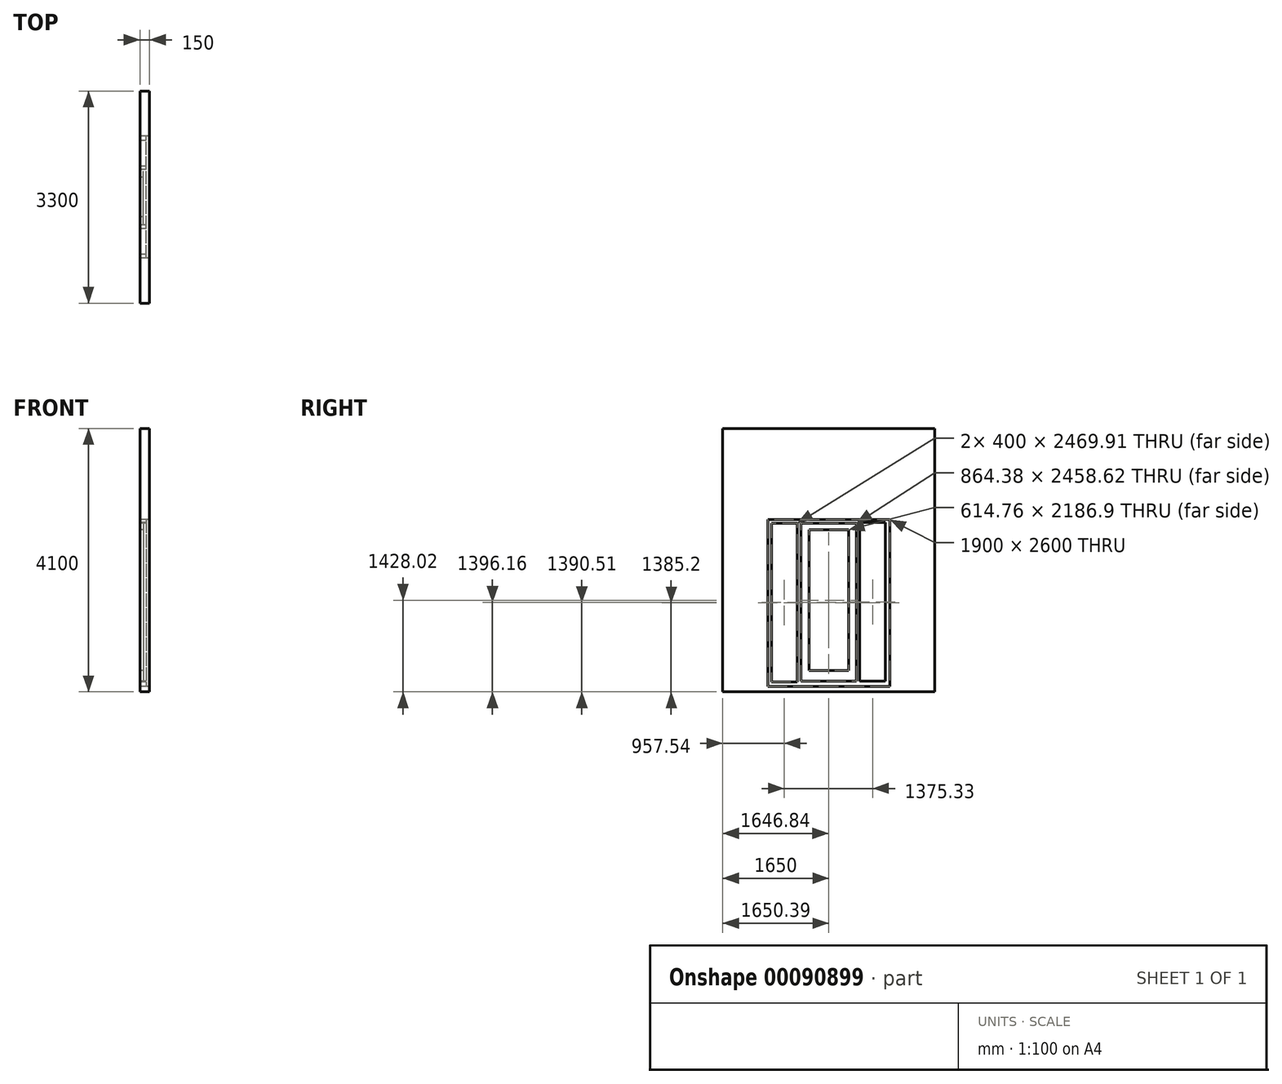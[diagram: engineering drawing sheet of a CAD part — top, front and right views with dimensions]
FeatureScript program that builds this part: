
annotation { "Feature Type Name" : "Feature", "Feature Type Description" : "" }
export const myFeature = defineFeature(function(context is Context, id is Id, definition is map)
    precondition{}
    {
        {
            var Q0;
            Q0=qCreatedBy(makeId("Right.planeOp"),FACE);
            var sketch = newSketch(context, id + "F0", { "sketchPlane" : qUnion([Q0])});
            skLineSegment(sketch, "E0.bottom", {"start": v(-1647.84, 2122.17) * mm, "end": v(1652.16, 2122.17) * mm});
            skLineSegment(sketch, "E0.top", {"start": v(-1647.84, -1977.83) * mm, "end": v(1652.16, -1977.83) * mm});
            skLineSegment(sketch, "E0.left", {"start": v(-1647.84, 2122.17) * mm, "end": v(-1647.84, -1977.83) * mm});
            skLineSegment(sketch, "E0.right", {"start": v(1652.16, 2122.17) * mm, "end": v(1652.16, -1977.83) * mm});
            skLineSegment(sketch, "E1.bottom", {"start": v(-947.84, 707.37) * mm, "end": v(952.16, 707.37) * mm});
            skLineSegment(sketch, "E1.top", {"start": v(-947.84, -1892.63) * mm, "end": v(952.16, -1892.63) * mm});
            skLineSegment(sketch, "E1.left", {"start": v(-947.84, 707.37) * mm, "end": v(-947.84, -1892.63) * mm});
            skLineSegment(sketch, "E1.right", {"start": v(952.16, 707.37) * mm, "end": v(952.16, -1892.63) * mm});
            skLineSegment(sketch, "E2.bottom", {"start": v(-890.3, 647.64) * mm, "end": v(-490.3, 647.64) * mm});
            skLineSegment(sketch, "E2.top", {"start": v(-890.3, -1822.27) * mm, "end": v(-490.3, -1822.27) * mm});
            skLineSegment(sketch, "E2.left", {"start": v(-890.3, 647.64) * mm, "end": v(-890.3, -1822.27) * mm});
            skLineSegment(sketch, "E2.right", {"start": v(-490.3, 647.64) * mm, "end": v(-490.3, -1822.27) * mm});
            skLineSegment(sketch, "E3.bottom", {"start": v(485.03, 658.92) * mm, "end": v(885.03, 658.92) * mm});
            skLineSegment(sketch, "E3.top", {"start": v(485.03, -1810.99) * mm, "end": v(885.03, -1810.99) * mm});
            skLineSegment(sketch, "E3.left", {"start": v(485.03, 658.92) * mm, "end": v(485.03, -1810.99) * mm});
            skLineSegment(sketch, "E3.right", {"start": v(885.03, 658.92) * mm, "end": v(885.03, -1810.99) * mm});
            skLineSegment(sketch, "E4.bottom", {"start": v(-433.18, 647.64) * mm, "end": v(431.2, 647.64) * mm});
            skLineSegment(sketch, "E4.top", {"start": v(-433.18, -1810.99) * mm, "end": v(431.2, -1810.99) * mm});
            skLineSegment(sketch, "E4.left", {"start": v(-433.18, 647.64) * mm, "end": v(-433.18, -1810.99) * mm});
            skLineSegment(sketch, "E4.right", {"start": v(431.2, 647.64) * mm, "end": v(431.2, -1810.99) * mm});
            skLineSegment(sketch, "E5.bottom", {"start": v(-304.83, 543.64) * mm, "end": v(309.93, 543.64) * mm});
            skLineSegment(sketch, "E5.top", {"start": v(-304.83, -1643.27) * mm, "end": v(309.93, -1643.27) * mm});
            skLineSegment(sketch, "E5.left", {"start": v(-304.83, 543.64) * mm, "end": v(-304.83, -1643.27) * mm});
            skLineSegment(sketch, "E5.right", {"start": v(309.93, 543.64) * mm, "end": v(309.93, -1643.27) * mm});
            skSolve(sketch);
        }
        {
            var Q0;
            Q0=makeQuery(id+"F0.imprint","IMPRINT",FACE,{"disambiguationData":[TD([[makeQuery(id+"F0.imprint","IMPRINT",EDGE,{"derivedFrom":sQuery(id+"F0.wireOp",EDGE,"E0.bottom")}),-1.0]])]});
            extrude(context, id + "F1", {"entities" : qUnion([Q0]), "depth" : 150 * mm});
        }
        {
            var Q0;
            Q0=makeQuery(id+"F0.imprint","IMPRINT",FACE,{"disambiguationData":[TD([[makeQuery(id+"F0.imprint","IMPRINT",EDGE,{"derivedFrom":sQuery(id+"F0.wireOp",EDGE,"E1.bottom")}),-1.0]])]});
            extrude(context, id + "F2", {"entities" : qUnion([Q0]), "depth" : 100 * mm});
        }
        {
            var Q0;
            Q0=makeQuery(id+"F0.imprint","IMPRINT",FACE,{"disambiguationData":[TD([[makeQuery(id+"F0.imprint","IMPRINT",EDGE,{"derivedFrom":sQuery(id+"F0.wireOp",EDGE,"E4.bottom")}),-1.0]])]});
            extrude(context, id + "F3", {"entities" : qUnion([Q0]), "depth" : 50 * mm});
        }
    });
